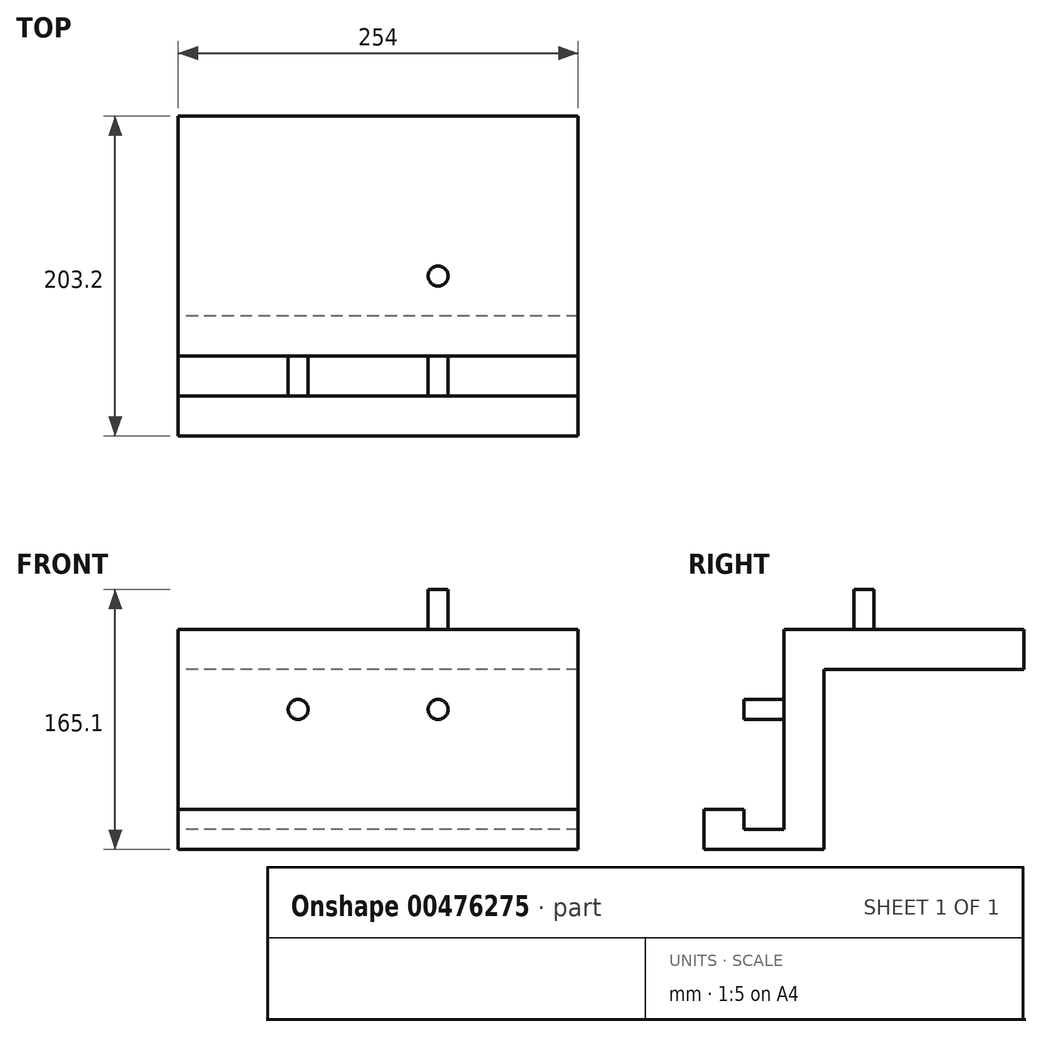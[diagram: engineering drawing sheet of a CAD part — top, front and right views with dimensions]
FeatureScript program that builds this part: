
annotation { "Feature Type Name" : "Feature", "Feature Type Description" : "" }
export const myFeature = defineFeature(function(context is Context, id is Id, definition is map)
    precondition{}
    {
        {
            var Q0;
            Q0=qCreatedBy(makeId("Front.planeOp"),FACE);
            var sketch = newSketch(context, id + "F0", { "sketchPlane" : qUnion([Q0])});
            skLineSegment(sketch, "E0.bottom", {"start": v(127, 76.2) * mm, "end": v(-127, 76.2) * mm});
            skLineSegment(sketch, "E0.top", {"start": v(127, -76.2) * mm, "end": v(-127, -76.2) * mm});
            skLineSegment(sketch, "E0.left", {"start": v(127, 76.2) * mm, "end": v(127, -76.2) * mm});
            skLineSegment(sketch, "E0.right", {"start": v(-127, 76.2) * mm, "end": v(-127, -76.2) * mm});
            skPoint(sketch, "E0.middle", {"position": v(0, 0) * mm});
            skCircle(sketch, "E1", {"center": v(38.1, 0) * mm, "radius": 6.35 * mm});
            skCircle(sketch, "E2", {"center": v(38.1, 0) * mm, "radius": 63.5 * mm, "construction": true});
            skCircle(sketch, "E3", {"center": v(38.1, 0) * mm, "radius": 50.8 * mm, "construction": true});
            skCircle(sketch, "E4", {"center": v(-50.8, 0) * mm, "radius": 25.4 * mm, "construction": true});
            skCircle(sketch, "E5", {"center": v(-50.8, 0) * mm, "radius": 38.1 * mm, "construction": true});
            skCircle(sketch, "E6", {"center": v(-50.8, 0) * mm, "radius": 6.35 * mm});
            skSolve(sketch);
        }
        {
            var Q0;
            Q0=makeQuery(id+"F0.imprint","IMPRINT",FACE,{"disambiguationData":[TD([[makeQuery(id+"F0.imprint","IMPRINT",EDGE,{"derivedFrom":sQuery(id+"F0.wireOp",EDGE,"E0.bottom")}),1.0]])]});
            extrude(context, id + "F1", {"entities" : qUnion([Q0]), "depth" : 25.4 * mm});
        }
        {
            var Q0;
            Q0=makeQuery(id+"F0.imprint","IMPRINT",FACE,{"disambiguationData":[TD([[makeQuery(id+"F0.imprint","IMPRINT",EDGE,{"derivedFrom":sQuery(id+"F0.wireOp",EDGE,"E1")}),1.0]])]});
            var Q1;
            Q1=makeQuery(id+"F0.imprint","IMPRINT",FACE,{"disambiguationData":[TD([[makeQuery(id+"F0.imprint","IMPRINT",EDGE,{"derivedFrom":sQuery(id+"F0.wireOp",EDGE,"E6")}),1.0]])]});
            extrude(context, id + "F2", {"entities" : qUnion([Q0, Q1]), "operationType" : NewBodyOperationType.ADD, "depth" : 50.8 * mm});
        }
        {
            var Q0;
            Q0=makeQuery(id+"F1.opExtrude","CAP_FACE",FACE,{"disambiguationData":[OSD([sQuery(id+"F0.wireOp",EDGE,"E0.bottom"),sQuery(id+"F0.wireOp",EDGE,"E0.top"),sQuery(id+"F0.wireOp",EDGE,"E0.left"),sQuery(id+"F0.wireOp",EDGE,"E0.right"),sQuery(id+"F0.wireOp",EDGE,"E1"),sQuery(id+"F0.wireOp",EDGE,"E6")])],"isStart":false});
            var sketch = newSketch(context, id + "F3", { "sketchPlane" : qUnion([Q0])});
            skLineSegment(sketch, "E7.bottom", {"start": v(-127, -76.2) * mm, "end": v(127, -76.2) * mm});
            skLineSegment(sketch, "E7.top", {"start": v(-127, -50.8) * mm, "end": v(127, -50.8) * mm});
            skLineSegment(sketch, "E7.left", {"start": v(-127, -76.2) * mm, "end": v(-127, -50.8) * mm});
            skLineSegment(sketch, "E7.right", {"start": v(127, -76.2) * mm, "end": v(127, -50.8) * mm});
            skLineSegment(sketch, "E8.bottom", {"start": v(127, -76.2) * mm, "end": v(-127, -76.2) * mm});
            skLineSegment(sketch, "E8.top", {"start": v(127, -63.5) * mm, "end": v(-127, -63.5) * mm});
            skLineSegment(sketch, "E8.left", {"start": v(127, -76.2) * mm, "end": v(127, -63.5) * mm});
            skLineSegment(sketch, "E8.right", {"start": v(-127, -76.2) * mm, "end": v(-127, -63.5) * mm});
            skLineSegment(sketch, "E9.top", {"start": v(-127, -88.9) * mm, "end": v(127, -88.9) * mm});
            skLineSegment(sketch, "E9.left", {"start": v(-127, -76.2) * mm, "end": v(-127, -88.9) * mm});
            skLineSegment(sketch, "E9.right", {"start": v(127, -76.2) * mm, "end": v(127, -88.9) * mm});
            skSolve(sketch);
        }
        {
            var Q0;
            Q0=makeQuery(id+"F3.imprint","IMPRINT",FACE,{"disambiguationData":[TD([[makeQuery(id+"F3.imprint","IMPRINT",EDGE,{"derivedFrom":sQuery(id+"F3.wireOp",EDGE,"E7.bottom")}),1.0]])]});
            var Q1;
            Q1=sQuery(id+"F0.wireOp",VERTEX,"E0.right.end");
            extrude(context, id + "F4", {"entities" : qUnion([Q0]), "operationType" : NewBodyOperationType.ADD, "endBound" : BoundingType.SYMMETRIC, "oppositeDirection" : true, "endBoundEntityVertex" : qUnion([Q1]), "depth" : 50.8 * mm});
        }
        {
            var Q0;
            Q0=makeQuery(id+"F4.opExtrude","CAP_FACE",FACE,{"disambiguationData":[OSD([sQuery(id+"F3.wireOp",EDGE,"E7.bottom"),sQuery(id+"F3.wireOp",EDGE,"E9.top"),sQuery(id+"F3.wireOp",EDGE,"E9.left"),sQuery(id+"F3.wireOp",EDGE,"E9.right")])],"isStart":true});
            var sketch = newSketch(context, id + "F5", { "sketchPlane" : qUnion([Q0])});
            skLineSegment(sketch, "E10.bottom", {"start": v(-127, -88.9) * mm, "end": v(127, -88.9) * mm});
            skLineSegment(sketch, "E10.top", {"start": v(-127, -63.5) * mm, "end": v(127, -63.5) * mm});
            skLineSegment(sketch, "E10.left", {"start": v(-127, -88.9) * mm, "end": v(-127, -63.5) * mm});
            skLineSegment(sketch, "E10.right", {"start": v(127, -88.9) * mm, "end": v(127, -63.5) * mm});
            skSolve(sketch);
        }
        {
            var Q0;
            Q0 = qSketchRegion(id + "F5", true);
            extrude(context, id + "F6", {"entities" : qUnion([Q0]), "operationType" : NewBodyOperationType.ADD, "depth" : 25.4 * mm});
        }
        {
            var Q0;
            Q0=makeQuery(id+"F1.opExtrude","SWEPT_FACE",FACE,{"disambiguationData":[OSD([sQuery(id+"F0.wireOp",EDGE,"E0.bottom")])]});
            var sketch = newSketch(context, id + "F7", { "sketchPlane" : qUnion([Q0])});
            skLineSegment(sketch, "E11.bottom", {"start": v(-127, 0) * mm, "end": v(127, 0) * mm});
            skLineSegment(sketch, "E11.top", {"start": v(-127, -25.4) * mm, "end": v(127, -25.4) * mm});
            skLineSegment(sketch, "E11.left", {"start": v(-127, 0) * mm, "end": v(-127, -25.4) * mm});
            skLineSegment(sketch, "E11.right", {"start": v(127, 0) * mm, "end": v(127, -25.4) * mm});
            skSolve(sketch);
        }
        {
            var Q0;
            Q0 = qSketchRegion(id + "F7", true);
            extrude(context, id + "F8", {"entities" : qUnion([Q0]), "operationType" : NewBodyOperationType.REMOVE, "oppositeDirection" : true, "depth" : 25.4 * mm});
        }
        {
            var Q0;
            {var subQ0=sQuery(id+"F0.wireOp",EDGE,"E6");var subQ1=sQuery(id+"F0.wireOp",EDGE,"E1");Q0=makeQuery(id+"F4.boolean.opBoolean","MERGE",FACE,{"derivedFrom":[makeQuery(id+"F2.boolean.opBoolean","MERGE",FACE,{"derivedFrom":[makeQuery(id+"F1.opExtrude","CAP_FACE",FACE,{"disambiguationData":[OSD([sQuery(id+"F0.wireOp",EDGE,"E0.bottom"),sQuery(id+"F0.wireOp",EDGE,"E0.top"),sQuery(id+"F0.wireOp",EDGE,"E0.left"),sQuery(id+"F0.wireOp",EDGE,"E0.right"),subQ1,subQ0])],"isStart":true}),makeQuery(id+"F2.opExtrude","CAP_FACE",FACE,{"disambiguationData":[OSD([subQ1])],"isStart":true}),makeQuery(id+"F2.opExtrude","CAP_FACE",FACE,{"disambiguationData":[OSD([subQ0])],"isStart":true})]}),makeQuery(id+"F4.opExtrude","CAP_FACE",FACE,{"disambiguationData":[OSD([sQuery(id+"F3.wireOp",EDGE,"E7.bottom"),sQuery(id+"F3.wireOp",EDGE,"E9.top"),sQuery(id+"F3.wireOp",EDGE,"E9.left"),sQuery(id+"F3.wireOp",EDGE,"E9.right")])],"isStart":false})]});}
            var sketch = newSketch(context, id + "F9", { "sketchPlane" : qUnion([Q0])});
            skLineSegment(sketch, "E12.bottom", {"start": v(-127, 50.8) * mm, "end": v(127, 50.8) * mm});
            skLineSegment(sketch, "E12.top", {"start": v(-127, 25.4) * mm, "end": v(127, 25.4) * mm});
            skLineSegment(sketch, "E12.left", {"start": v(-127, 50.8) * mm, "end": v(-127, 25.4) * mm});
            skLineSegment(sketch, "E12.right", {"start": v(127, 50.8) * mm, "end": v(127, 25.4) * mm});
            skSolve(sketch);
        }
        {
            var Q0;
            Q0 = qSketchRegion(id + "F9", true);
            extrude(context, id + "F10", {"entities" : qUnion([Q0]), "operationType" : NewBodyOperationType.ADD, "depth" : 127 * mm});
        }
        {
            var Q0;
            Q0=makeQuery(id+"F10.boolean.opBoolean","MERGE",FACE,{"derivedFrom":[makeQuery(id+"F8.boolean.opBoolean","COPY",FACE,{"derivedFrom":makeQuery(id+"F8.opExtrude","CAP_FACE",FACE,{"disambiguationData":[OSD([sQuery(id+"F7.wireOp",EDGE,"E11.bottom"),sQuery(id+"F7.wireOp",EDGE,"E11.top"),sQuery(id+"F7.wireOp",EDGE,"E11.left"),sQuery(id+"F7.wireOp",EDGE,"E11.right")])],"isStart":false})}),makeQuery(id+"F10.opExtrude","SWEPT_FACE",FACE,{"disambiguationData":[OSD([sQuery(id+"F9.wireOp",EDGE,"E12.bottom")])]})]});
            var sketch = newSketch(context, id + "F11", { "sketchPlane" : qUnion([Q0])});
            skLineSegment(sketch, "E13", {"start": v(0, 0) * mm, "end": v(38.1, 0) * mm});
            skLineSegment(sketch, "E14", {"start": v(38.1, 0) * mm, "end": v(38.1, 25.4) * mm});
            skCircle(sketch, "E15", {"center": v(38.1, 25.4) * mm, "radius": 6.35 * mm});
            skLineSegment(sketch, "E16", {"start": v(38.1, -25.4) * mm, "end": v(38.1, 25.4) * mm});
            skSolve(sketch);
        }
        {
            var Q0;
            Q0=makeQuery(id+"F11.imprint","IMPRINT",FACE,{"disambiguationData":[TD([[makeQuery(id+"F11.imprint","IMPRINT",EDGE,{"derivedFrom":sQuery(id+"F11.wireOp",EDGE,"E15")}),1.0]])]});
            extrude(context, id + "F12", {"entities" : qUnion([Q0]), "operationType" : NewBodyOperationType.ADD, "depth" : 25.4 * mm});
        }
    });
